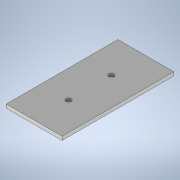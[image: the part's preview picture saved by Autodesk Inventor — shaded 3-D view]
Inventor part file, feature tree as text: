
AUTODESK INVENTOR PART (.ipt)
format: ipt  version: 2022 (Build 260153000, 153)  size: 105,472 bytes
history: native  units: mm
features: sketch x1, extrude x1, hole x1
ambient origin geometry x8: Origin, YZ Plane, XZ Plane, XY Plane, X Axis, Y Axis, Z Axis, Center Point
bodies: Solid1 (feature_tree)
feature tree (3):
  sketch  "Sketch1"  dims[d0=30.0mm d1=60.0mm d2=30.0mm d3=15.0mm d4=23.0mm d5=18.5mm d6=2.0mm d7=0.0mm d8=2.8mm d9=6.0mm d10=5.0mm d11=0.5mm d12=90.0deg d13=8.0mm d14=20.594885mm]
  extrude  "Extrusion1"  Depth=60.0mm
  hole  "Hole1"  [1 undecoded]
note: 1 required parameter value undecoded (feature->parameter linkage not recoverable at this tier; creation-order binding heuristic only, values carry confidence <= 0.55)
